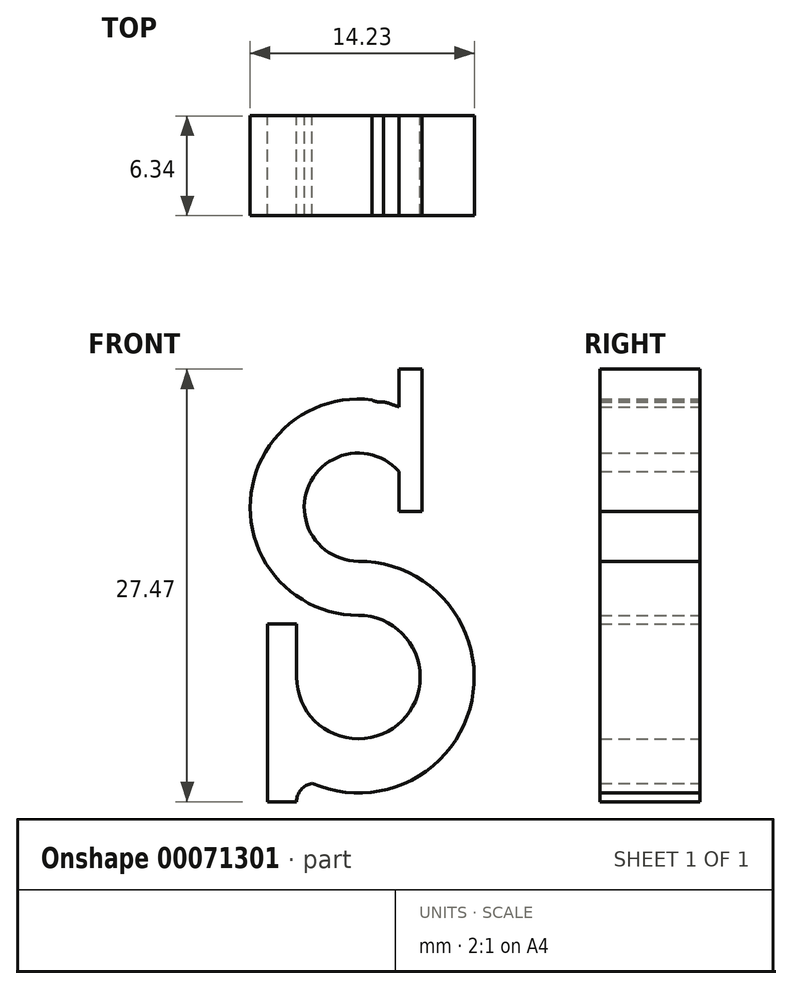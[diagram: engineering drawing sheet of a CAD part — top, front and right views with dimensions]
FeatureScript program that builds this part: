
annotation { "Feature Type Name" : "Feature", "Feature Type Description" : "" }
export const myFeature = defineFeature(function(context is Context, id is Id, definition is map)
    precondition{}
    {
        {
            var Q0;
            Q0=qCreatedBy(makeId("Front.planeOp"),FACE);
            var sketch = newSketch(context, id + "F0", { "sketchPlane" : qUnion([Q0])});
            skArc(sketch, "E0", {"start": v(0, 0) * mm, "mid": v(-6.26, 9.7) * mm, "end": v(5.15, 11.42) * mm});
            skArc(sketch, "E1", {"start": v(0, -6.87) * mm, "mid": v(-13.3, 10.32) * mm, "end": v(6.67, 18.88) * mm});
            skArc(sketch, "E2", {"start": v(0, 0) * mm, "mid": v(13.26, -21.12) * mm, "end": v(-11.53, -23.87) * mm});
            skArc(sketch, "E3", {"start": v(0, -6.87) * mm, "mid": v(5.55, -20.27) * mm, "end": v(-7.85, -14.72) * mm});
            skLineSegment(sketch, "E4.bottom", {"start": v(5.15, 6.3) * mm, "end": v(8.06, 6.3) * mm});
            skLineSegment(sketch, "E4.top", {"start": v(5.15, 24.4) * mm, "end": v(8.06, 24.4) * mm});
            skLineSegment(sketch, "E4.left", {"start": v(5.15, 6.3) * mm, "end": v(5.15, 24.4) * mm});
            skLineSegment(sketch, "E4.right", {"start": v(8.06, 6.3) * mm, "end": v(8.06, 24.4) * mm});
            skLineSegment(sketch, "E5.bottom", {"start": v(-7.85, -8) * mm, "end": v(-11.53, -8) * mm});
            skLineSegment(sketch, "E5.top", {"start": v(-7.85, -30.55) * mm, "end": v(-11.53, -30.55) * mm});
            skLineSegment(sketch, "E5.left", {"start": v(-7.85, -8) * mm, "end": v(-7.85, -30.55) * mm});
            skLineSegment(sketch, "E5.right", {"start": v(-11.53, -8) * mm, "end": v(-11.53, -30.55) * mm});
            skArc(sketch, "E6", {"start": v(1.72, 20.5) * mm, "mid": v(3.97, 20.5) * mm, "end": v(5.15, 22.43) * mm});
            skArc(sketch, "E7", {"start": v(-5.86, -28.22) * mm, "mid": v(-7.29, -29.02) * mm, "end": v(-7.85, -30.55) * mm});
            skSolve(sketch);
        }
        {
            var Q0;
            {var subQ4=sQuery(id+"F0.wireOp",EDGE,"E5.bottom");Q0=makeQuery(id+"F0.imprint","IMPRINT",FACE,{"disambiguationData":[TD([[makeQuery(id+"F0.imprint","IMPRINT",EDGE,{"derivedFrom":subQ4}),1.0]])]});}
            var Q1;
            {var subQ5=sQuery(id+"F0.wireOp",EDGE,"E5.top");Q1=makeQuery(id+"F0.imprint","IMPRINT",FACE,{"disambiguationData":[TD([[makeQuery(id+"F0.imprint","IMPRINT",EDGE,{"derivedFrom":subQ5}),-1.0]])]});}
            var Q2;
            {var subQ3=sQuery(id+"F0.wireOp",EDGE,"E4.bottom");Q2=makeQuery(id+"F0.imprint","IMPRINT",FACE,{"disambiguationData":[TD([[makeQuery(id+"F0.imprint","IMPRINT",EDGE,{"derivedFrom":subQ3}),1.0]])]});}
            var Q3;
            {var subQ1=sQuery(id+"F0.wireOp",EDGE,"E0");Q3=makeQuery(id+"F0.imprint","IMPRINT",FACE,{"disambiguationData":[TD([[makeQuery(id+"F0.imprint","IMPRINT",EDGE,{"derivedFrom":subQ1}),1.0]])]});}
            var Q4;
            {var subQ0=sQuery(id+"F0.wireOp",EDGE,"E6");var subQ1=sQuery(id+"F0.wireOp",EDGE,"E1");var subQ2=makeQuery(id+"F0.imprint","INTERSECT",VERTEX,{"disambiguationData":[OD(0.0)],"derivedFrom":[subQ1,subQ0]});Q4=makeQuery(id+"F0.imprint","IMPRINT",FACE,{"disambiguationData":[TD([[makeQuery(id+"F0.imprint","IMPRINT",EDGE,{"disambiguationData":[TD([[subQ2,-1.0]])],"derivedFrom":subQ1}),-1.0]])]});}
            var Q5;
            {var subQ0=sQuery(id+"F0.wireOp",EDGE,"E6");var subQ1=sQuery(id+"F0.wireOp",EDGE,"E1");var subQ2=makeQuery(id+"F0.imprint","INTERSECT",VERTEX,{"disambiguationData":[OD(1.0)],"derivedFrom":[subQ1,subQ0]});Q5=makeQuery(id+"F0.imprint","IMPRINT",FACE,{"disambiguationData":[TD([[makeQuery(id+"F0.imprint","IMPRINT",EDGE,{"disambiguationData":[TD([[subQ2,-1.0]])],"derivedFrom":subQ1}),1.0]])]});}
            var Q6;
            {var subQ0=sQuery(id+"F0.wireOp",EDGE,"E7");Q6=makeQuery(id+"F0.imprint","IMPRINT",FACE,{"disambiguationData":[TD([[makeQuery(id+"F0.imprint","IMPRINT",EDGE,{"derivedFrom":subQ0}),-1.0]])]});}
            extrude(context, id + "F1", {"entities" : qUnion([Q0, Q1, Q2, Q3, Q4, Q5, Q6]), "endBound" : BoundingType.SYMMETRIC, "depth" : 12.7 * mm});
        }
        {
            var Q0;
            Q0=makeQuery(id+"F1.opExtrude","SWEPT_BODY",BODY,{"disambiguationData":[OSD([sQuery(id+"F0.wireOp",EDGE,"E0"),sQuery(id+"F0.wireOp",EDGE,"E1"),sQuery(id+"F0.wireOp",EDGE,"E2"),sQuery(id+"F0.wireOp",EDGE,"E3"),sQuery(id+"F0.wireOp",EDGE,"E4.bottom"),sQuery(id+"F0.wireOp",EDGE,"E4.top"),sQuery(id+"F0.wireOp",EDGE,"E4.left"),sQuery(id+"F0.wireOp",EDGE,"E4.right"),sQuery(id+"F0.wireOp",EDGE,"E5.bottom"),sQuery(id+"F0.wireOp",EDGE,"E5.top"),sQuery(id+"F0.wireOp",EDGE,"E5.left"),sQuery(id+"F0.wireOp",EDGE,"E5.right"),sQuery(id+"F0.wireOp",EDGE,"E6"),sQuery(id+"F0.wireOp",EDGE,"E7")])]});
            var Q1;
            Q1=qCreatedBy(makeId("Origin.pointOp"),VERTEX);
            transform(context, id + "F2", {"entities" : qUnion([Q0]), "transformType" : TransformType.SCALE_UNIFORMLY, "scale" : 0.5, "scalePoint" : qUnion([Q1]), "makeCopy" : false});
        }
    });
